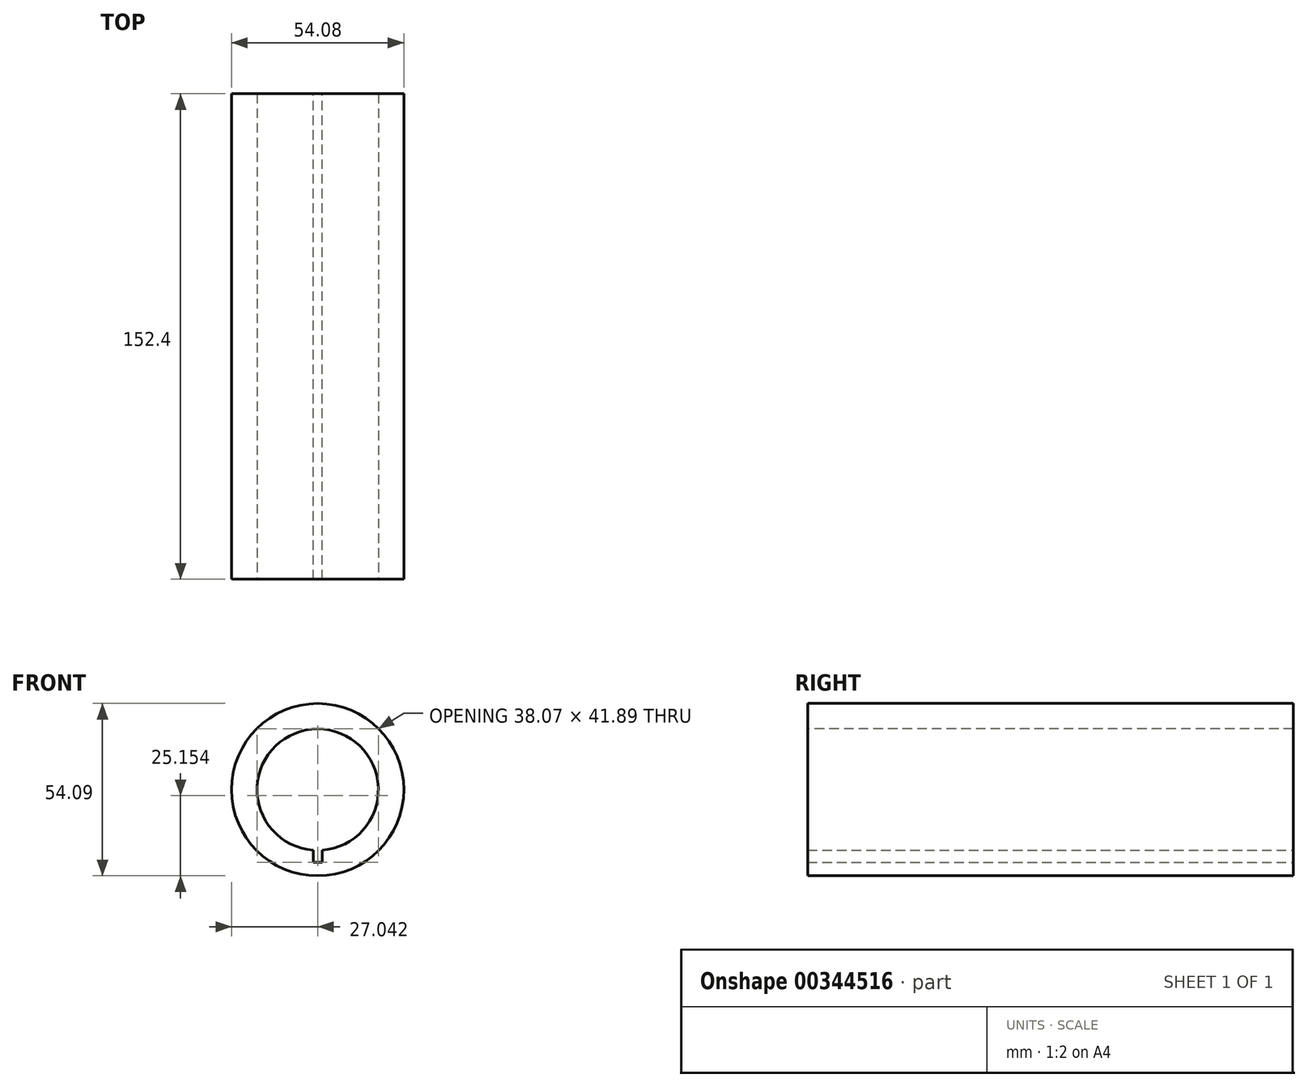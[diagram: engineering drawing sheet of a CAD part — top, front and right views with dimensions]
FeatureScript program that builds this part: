
annotation { "Feature Type Name" : "Feature", "Feature Type Description" : "" }
export const myFeature = defineFeature(function(context is Context, id is Id, definition is map)
    precondition{}
    {
        {
            var Q0;
            Q0=qCreatedBy(makeId("Front.planeOp"),FACE);
            var sketch = newSketch(context, id + "F0", { "sketchPlane" : qUnion([Q0])});
            skCircle(sketch, "E0", {"center": v(27.64, 27.88) * mm, "radius": 27.04 * mm});
            skSolve(sketch);
        }
        {
            var Q0;
            Q0=makeQuery(id+"F0.imprint","IMPRINT",FACE,{"disambiguationData":[TD([[makeQuery(id+"F0.imprint","IMPRINT",EDGE,{"derivedFrom":sQuery(id+"F0.wireOp",EDGE,"E0")}),1.0]])]});
            extrude(context, id + "F1", {"entities" : qUnion([Q0]), "depth" : 25.4 * mm});
        }
        {
            var Q0;
            Q0=makeQuery(id+"F1.opExtrude","CAP_FACE",FACE,{"disambiguationData":[OSD([sQuery(id+"F0.wireOp",EDGE,"E0")])],"isStart":false});
            var sketch = newSketch(context, id + "F2", { "sketchPlane" : qUnion([Q0])});
            skPoint(sketch, "E1", {"position": v(27.64, 27.88) * mm});
            skSolve(sketch);
        }
        {
            var Q0;
            Q0=sQuery(id+"F2.wireOp",VERTEX,"E1");
            var Q1;
            Q1=makeQuery(id+"F1.opExtrude","SWEPT_BODY",BODY,{"disambiguationData":[OSD([sQuery(id+"F0.wireOp",EDGE,"E0")])]});
            hole(context, id + "F3", {"style" : HoleStyle.SIMPLE, "endStyle" : HoleEndStyle.THROUGH, "holeDiameter" : 38.1 * mm, "isTappedThrough" : true, "tappedDepth" : 12.7 * mm, "tapClearance" : 3, "locations" : qUnion([Q0]), "scope" : qUnion([Q1])});
        }
        {
            var Q0;
            Q0=makeQuery(id+"F1.opExtrude","CAP_FACE",FACE,{"disambiguationData":[OSD([sQuery(id+"F0.wireOp",EDGE,"E0")])],"isStart":true});
            var sketch = newSketch(context, id + "F4", { "sketchPlane" : qUnion([Q0])});
            skLineSegment(sketch, "E2.bottom", {"start": v(-26.25, 8.88) * mm, "end": v(-29.02, 8.88) * mm});
            skLineSegment(sketch, "E2.top", {"start": v(-26.25, 5.04) * mm, "end": v(-29.02, 5.04) * mm});
            skLineSegment(sketch, "E2.left", {"start": v(-26.25, 8.88) * mm, "end": v(-26.25, 5.04) * mm});
            skLineSegment(sketch, "E2.right", {"start": v(-29.02, 8.88) * mm, "end": v(-29.02, 5.04) * mm});
            skSolve(sketch);
        }
        {
            var Q0;
            {var subQ0=sQuery(id+"F4.wireOp",EDGE,"E2.top");Q0=makeQuery(id+"F4.imprint","IMPRINT",FACE,{"disambiguationData":[TD([[makeQuery(id+"F4.imprint","IMPRINT",EDGE,{"derivedFrom":subQ0}),-1.0]])]});}
            extrude(context, id + "F5", {"entities" : qUnion([Q0]), "operationType" : NewBodyOperationType.REMOVE, "oppositeDirection" : true, "depth" : 25.4 * mm});
        }
        {
            var Q0;
            Q0=makeQuery(id+"F1.opExtrude","CAP_FACE",FACE,{"disambiguationData":[OSD([sQuery(id+"F0.wireOp",EDGE,"E0")])],"isStart":false});
            extrude(context, id + "F6", {"entities" : qUnion([Q0]), "operationType" : NewBodyOperationType.ADD, "depth" : 127 * mm});
        }
    });
